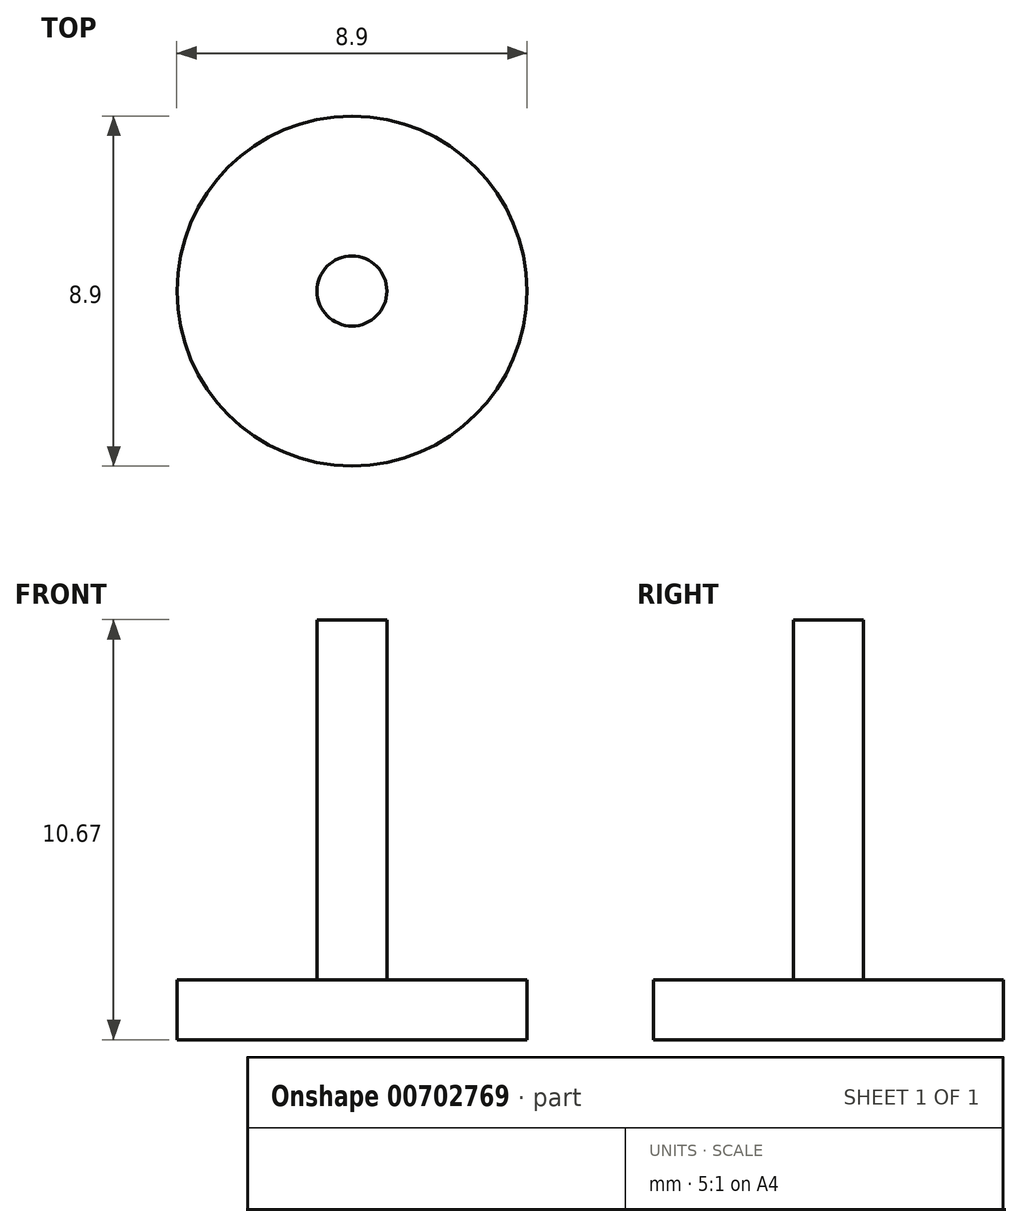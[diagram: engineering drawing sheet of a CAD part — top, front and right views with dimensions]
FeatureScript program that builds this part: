
annotation { "Feature Type Name" : "Feature", "Feature Type Description" : "" }
export const myFeature = defineFeature(function(context is Context, id is Id, definition is map)
    precondition{}
    {
        {
            var Q0;
            Q0=qCreatedBy(makeId("Top.planeOp"),FACE);
            var sketch = newSketch(context, id + "F0", { "sketchPlane" : qUnion([Q0])});
            skCircle(sketch, "E0", {"center": v(0, 0) * mm, "radius": 4.45 * mm});
            skSolve(sketch);
        }
        {
            var Q0;
            Q0=qCreatedBy(makeId("Top.planeOp"),FACE);
            var sketch = newSketch(context, id + "F1", { "sketchPlane" : qUnion([Q0])});
            skCircle(sketch, "E1", {"center": v(0, 0) * mm, "radius": 0.89 * mm});
            skSolve(sketch);
        }
        {
            var Q0;
            Q0=makeQuery(id+"F0.imprint","IMPRINT",FACE,{"disambiguationData":[TD([[makeQuery(id+"F0.imprint","IMPRINT",EDGE,{"derivedFrom":sQuery(id+"F0.wireOp",EDGE,"E0")}),1.0]])]});
            extrude(context, id + "F2", {"entities" : qUnion([Q0]), "depth" : 1.52 * mm, "offsetDistance" : 25.4 * mm});
        }
        {
            var Q0;
            Q0=makeQuery(id+"F1.imprint","IMPRINT",FACE,{"disambiguationData":[TD([[makeQuery(id+"F1.imprint","IMPRINT",EDGE,{"derivedFrom":sQuery(id+"F1.wireOp",EDGE,"E1")}),1.0]])]});
            extrude(context, id + "F3", {"entities" : qUnion([Q0]), "operationType" : NewBodyOperationType.ADD, "depth" : 10.67 * mm, "offsetDistance" : 25.4 * mm});
        }
    });
